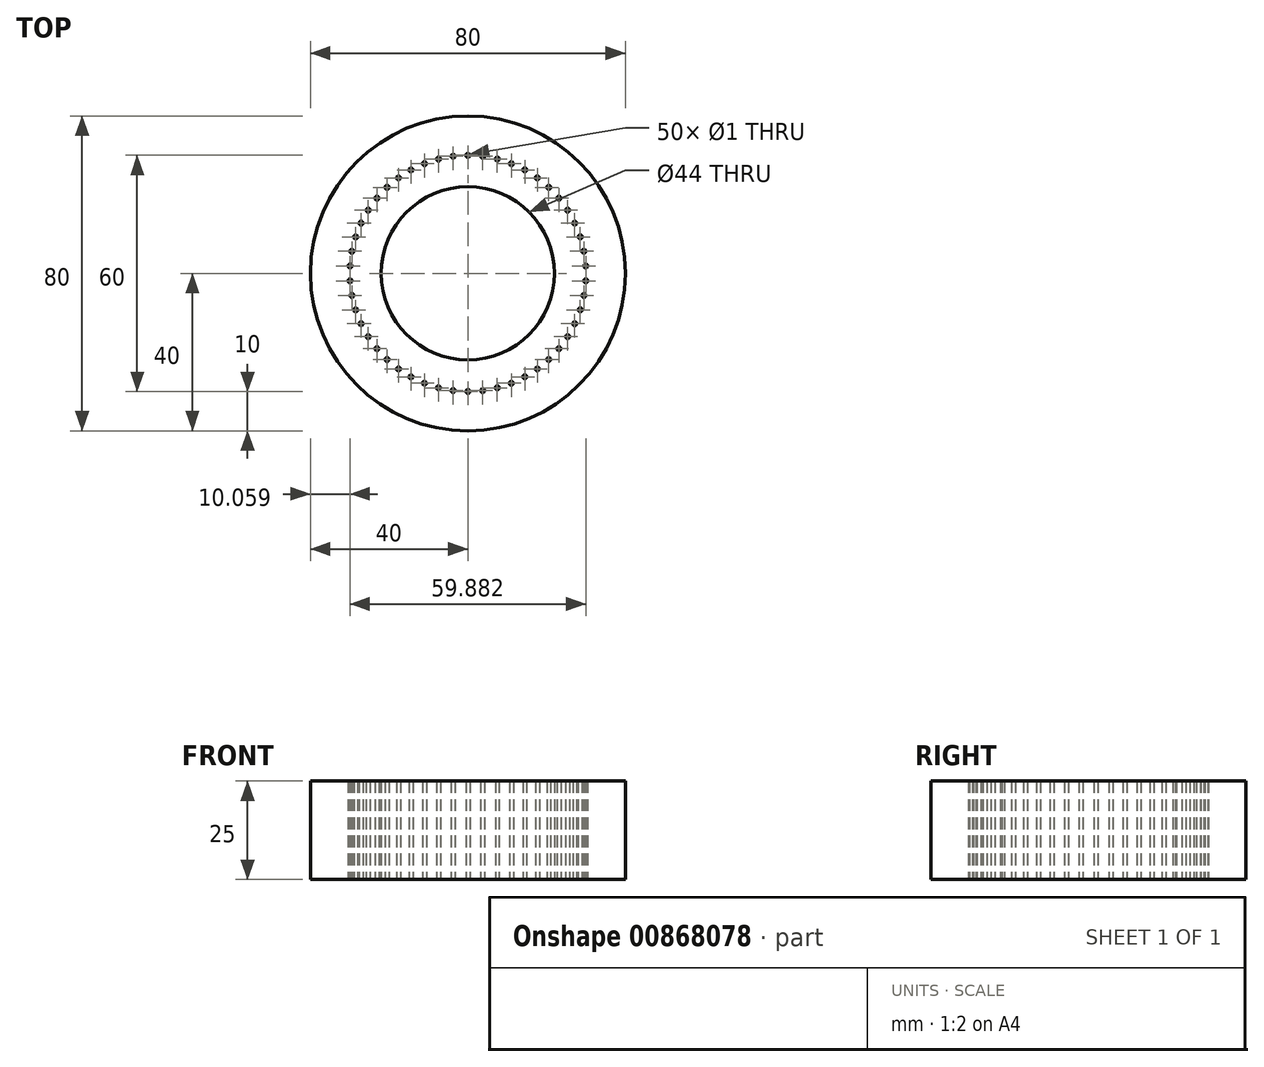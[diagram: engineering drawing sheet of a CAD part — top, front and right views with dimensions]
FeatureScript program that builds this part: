
annotation { "Feature Type Name" : "Feature", "Feature Type Description" : "" }
export const myFeature = defineFeature(function(context is Context, id is Id, definition is map)
    precondition{}
    {
        {
            var Q0;
            Q0=qCreatedBy(makeId("Top.planeOp"),FACE);
            var sketch = newSketch(context, id + "F0", { "sketchPlane" : qUnion([Q0])});
            skCircle(sketch, "E0", {"center": v(0, 0) * mm, "radius": 22 * mm});
            skCircle(sketch, "E1", {"center": v(0, 0) * mm, "radius": 40 * mm});
            skSolve(sketch);
        }
        {
            var Q0;
            Q0=makeQuery(id+"F0.imprint","IMPRINT",FACE,{"disambiguationData":[TD([[makeQuery(id+"F0.imprint","IMPRINT",EDGE,{"derivedFrom":sQuery(id+"F0.wireOp",EDGE,"E0")}),1.0]])]});
            extrude(context, id + "F1", {"entities" : qUnion([Q0]), "depth" : 25 * mm, "offsetDistance" : 25 * mm});
        }
        {
            var Q0;
            Q0=makeQuery(id+"F0.imprint","IMPRINT",FACE,{"disambiguationData":[TD([[makeQuery(id+"F0.imprint","IMPRINT",EDGE,{"derivedFrom":sQuery(id+"F0.wireOp",EDGE,"E0")}),-1.0]])]});
            extrude(context, id + "F2", {"entities" : qUnion([Q0]), "depth" : 25 * mm, "offsetDistance" : 25 * mm});
        }
        {
            var Q0;
            Q0=qCreatedBy(makeId("Top.planeOp"),FACE);
            var sketch = newSketch(context, id + "F3", { "sketchPlane" : qUnion([Q0])});
            skCircle(sketch, "E2", {"center": v(0, 0) * mm, "radius": 30 * mm, "construction": true});
            skCircle(sketch, "E3", {"center": v(0, 30) * mm, "radius": 0.5 * mm});
            skSolve(sketch);
        }
        {
            var Q0;
            Q0=makeQuery(id+"F3.imprint","IMPRINT",FACE,{"disambiguationData":[TD([[makeQuery(id+"F3.imprint","IMPRINT",EDGE,{"derivedFrom":sQuery(id+"F3.wireOp",EDGE,"E3")}),1.0]])]});
            extrude(context, id + "F4", {"entities" : qUnion([Q0]), "depth" : 25 * mm, "offsetDistance" : 25 * mm});
        }
        {
            var Q0;
            Q0=makeQuery(id+"F4.opExtrude","SWEPT_BODY",BODY,{"disambiguationData":[OSD([sQuery(id+"F3.wireOp",EDGE,"E3")])]});
            var Q1;
            Q1=makeQuery(id+"F2.opExtrude","CAP_EDGE",EDGE,{"disambiguationData":[OSD([sQuery(id+"F0.wireOp",EDGE,"E0")])],"isStart":false});
            circularPattern(context, id + "F5", {"operationType" : NewBodyOperationType.REMOVE, "entities" : qUnion([Q0]), "axis" : qUnion([Q1]), "angle" : 360 * degree, "instanceCount" : 50, "equalSpace" : true});
        }
    });
